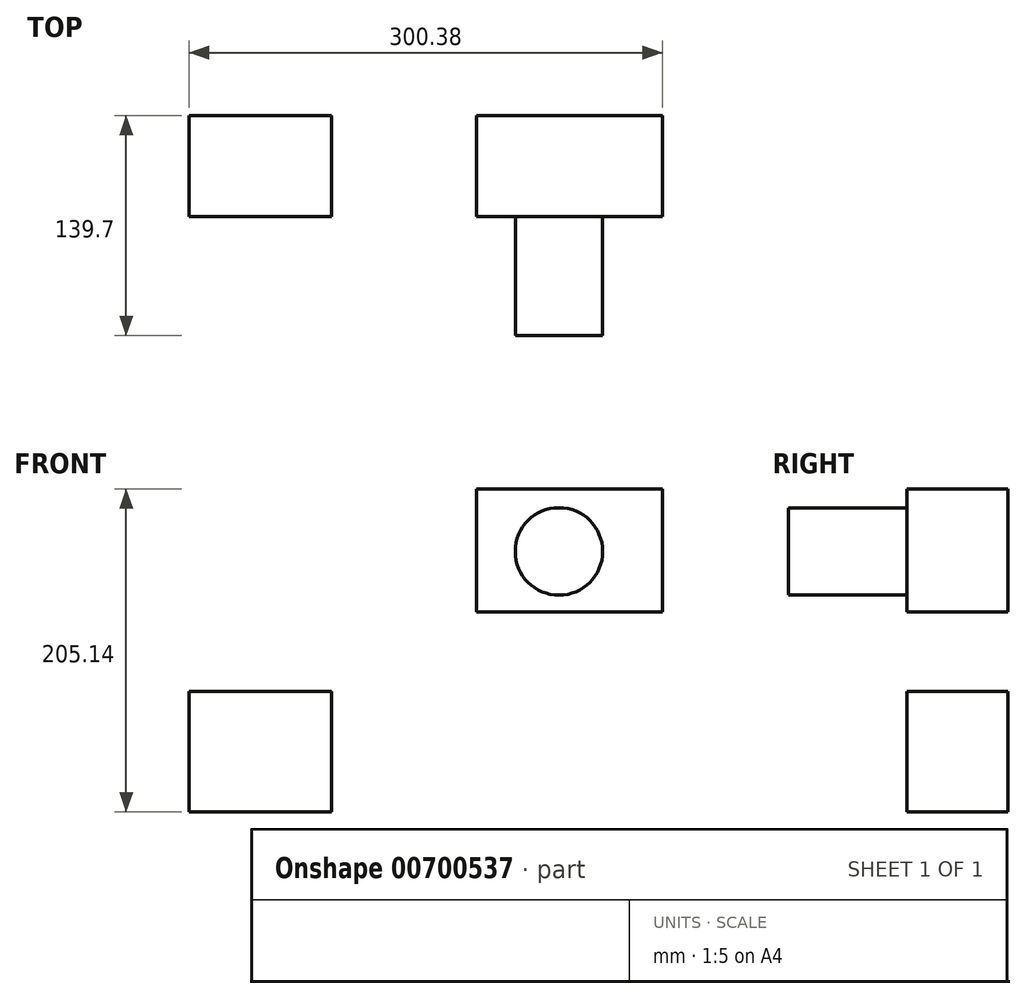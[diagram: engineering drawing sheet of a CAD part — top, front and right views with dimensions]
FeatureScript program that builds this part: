
annotation { "Feature Type Name" : "Feature", "Feature Type Description" : "" }
export const myFeature = defineFeature(function(context is Context, id is Id, definition is map)
    precondition{}
    {
        {
            var Q0;
            Q0=qCreatedBy(makeId("Front.planeOp"),FACE);
            var sketch = newSketch(context, id + "F0", { "sketchPlane" : qUnion([Q0])});
            skLineSegment(sketch, "E0.bottom", {"start": v(56.14, 107.5) * mm, "end": v(174.18, 107.5) * mm});
            skLineSegment(sketch, "E0.top", {"start": v(56.14, 29.36) * mm, "end": v(174.18, 29.36) * mm});
            skLineSegment(sketch, "E0.left", {"start": v(56.14, 107.5) * mm, "end": v(56.14, 29.36) * mm});
            skLineSegment(sketch, "E0.right", {"start": v(174.18, 107.5) * mm, "end": v(174.18, 29.36) * mm});
            skLineSegment(sketch, "E1.bottom", {"start": v(-126.2, -21.11) * mm, "end": v(-35.84, -21.11) * mm});
            skLineSegment(sketch, "E1.top", {"start": v(-126.2, -97.63) * mm, "end": v(-35.84, -97.63) * mm});
            skLineSegment(sketch, "E1.left", {"start": v(-126.2, -21.11) * mm, "end": v(-126.2, -97.63) * mm});
            skLineSegment(sketch, "E1.right", {"start": v(-35.84, -21.11) * mm, "end": v(-35.84, -97.63) * mm});
            skSolve(sketch);
        }
        {
            var Q0;
            Q0=makeQuery(id+"F0.imprint","IMPRINT",FACE,{"disambiguationData":[TD([[makeQuery(id+"F0.imprint","IMPRINT",EDGE,{"derivedFrom":sQuery(id+"F0.wireOp",EDGE,"E1.bottom")}),-1.0]])]});
            var Q1;
            Q1=makeQuery(id+"F0.imprint","IMPRINT",FACE,{"disambiguationData":[TD([[makeQuery(id+"F0.imprint","IMPRINT",EDGE,{"derivedFrom":sQuery(id+"F0.wireOp",EDGE,"E0.bottom")}),-1.0]])]});
            extrude(context, id + "F1", {"entities" : qUnion([Q0, Q1]), "depth" : 64.26 * mm, "offsetDistance" : 25.4 * mm});
        }
        {
            var Q0;
            Q0=makeQuery(id+"F1.opExtrude","CAP_FACE",FACE,{"disambiguationData":[OSD([sQuery(id+"F0.wireOp",EDGE,"E0.bottom"),sQuery(id+"F0.wireOp",EDGE,"E0.top"),sQuery(id+"F0.wireOp",EDGE,"E0.left"),sQuery(id+"F0.wireOp",EDGE,"E0.right")])],"isStart":false});
            var sketch = newSketch(context, id + "F2", { "sketchPlane" : qUnion([Q0])});
            skCircle(sketch, "E2", {"center": v(108.59, 67.84) * mm, "radius": 27.76 * mm});
            skSolve(sketch);
        }
        {
            var Q0;
            Q0 = qSketchRegion(id + "F2", true);
            extrude(context, id + "F3", {"entities" : qUnion([Q0]), "operationType" : NewBodyOperationType.ADD, "depth" : 75.44 * mm, "offsetDistance" : 25.4 * mm});
        }
    });
